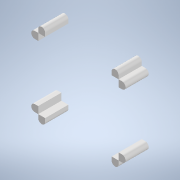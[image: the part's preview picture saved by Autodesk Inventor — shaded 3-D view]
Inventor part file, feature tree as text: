
AUTODESK INVENTOR PART (.ipt)
format: ipt  version: 2020 (Build 240168000, 168)  size: 230,400 bytes
history: native  units: in
note: dims shown in document units (in); Inventor stores cm internally (conversion verified against a paired STEP export)
features: reference x6, other x3, extrude x2, sketch x2, plane x1
ambient origin geometry x8: Origin, YZ Plane, XZ Plane, XY Plane, X Axis, Y Axis, Z Axis, Center Point
bodies: Solid1 (feature_tree)
feature tree (14):
  extrude  "Extrusion1"  Depth=0.15in
  plane  "Work Plane1"
  extrude  "Extrusion2"  Depth=0.15in
  sketch  "Sketch1"  dims[d0=0.15in d1=0.15in]
  reference  "Reference1"
  reference  "Reference2"
  reference  "Reference3"
  reference  "Reference4"
  reference  "Reference5"
  reference  "Reference6"
  sketch  "Sketch2"  dims[d2=0.15in d3=0.15in d4=0.15in d5=0.15in d6=0.15in d7=0.15in d8=0.15in d9=0.15in d10=0.15in d11=0.15in d12=0.15in d13=0.15in d14=0.15in d15=0.15in d16=0.075in d17=0.075in d18=0.075in d19=0.5in d20=0.0in d21=0.15in d22=0.15in d23=0.15in d24=0.15in d25=0.15in d26=0.15in d27=0.15in d28=0.15in d29=0.15in d30=0.15in d31=0.15in d32=0.15in d33=0.15in d34=0.15in d35=0.15in d36=0.15in d37=0.075in d38=0.075in d39=0.075in d40=0.1in d41=0.0in]
  other  "<userpath>\Documents\Inventor\Drone\Assembly.iam"
  other  "Assembly.iam"
  other  "Pixfalcon-Flight-Controller v1:1"
